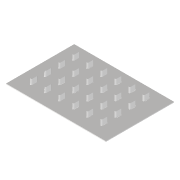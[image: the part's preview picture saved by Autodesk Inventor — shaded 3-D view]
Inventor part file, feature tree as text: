
AUTODESK INVENTOR PART (.ipt)
format: ipt  version: 2022 (Build 260153000, 153)  size: 3,466,240 bytes
history: native  units: mm
features: extrude x2, sketch x2, pattern_linear x1, projected_geometry x1
ambient origin geometry x8: Origin, YZ Plane, XZ Plane, XY Plane, X Axis, Y Axis, Z Axis, Center Point
bodies: Volumenkörper1 (feature_tree)
feature tree (6):
  extrude  "Extrusion1"  Depth=1.0mm
  extrude  "Extrusion2"  Depth=8.55mm
  pattern_linear  "Rechteckige Anordnung1"  Spacing1=4.275mm  [1 undecoded]
  sketch  "Skizze5"  dims[d2=1.0mm d3=0.0mm d4=8.1mm]
  sketch  "Skizze6"  dims[d5=2.2mm d6=8.55mm d7=4.275mm d8=7.0mm d9=0.0mm d10=40.0mm d12=18.7mm d13=60.0mm d15=18.7mm]
  projected_geometry  "Projizierte Kontur1"
note: 1 required parameter value undecoded (feature->parameter linkage not recoverable at this tier; creation-order binding heuristic only, values carry confidence <= 0.55)
